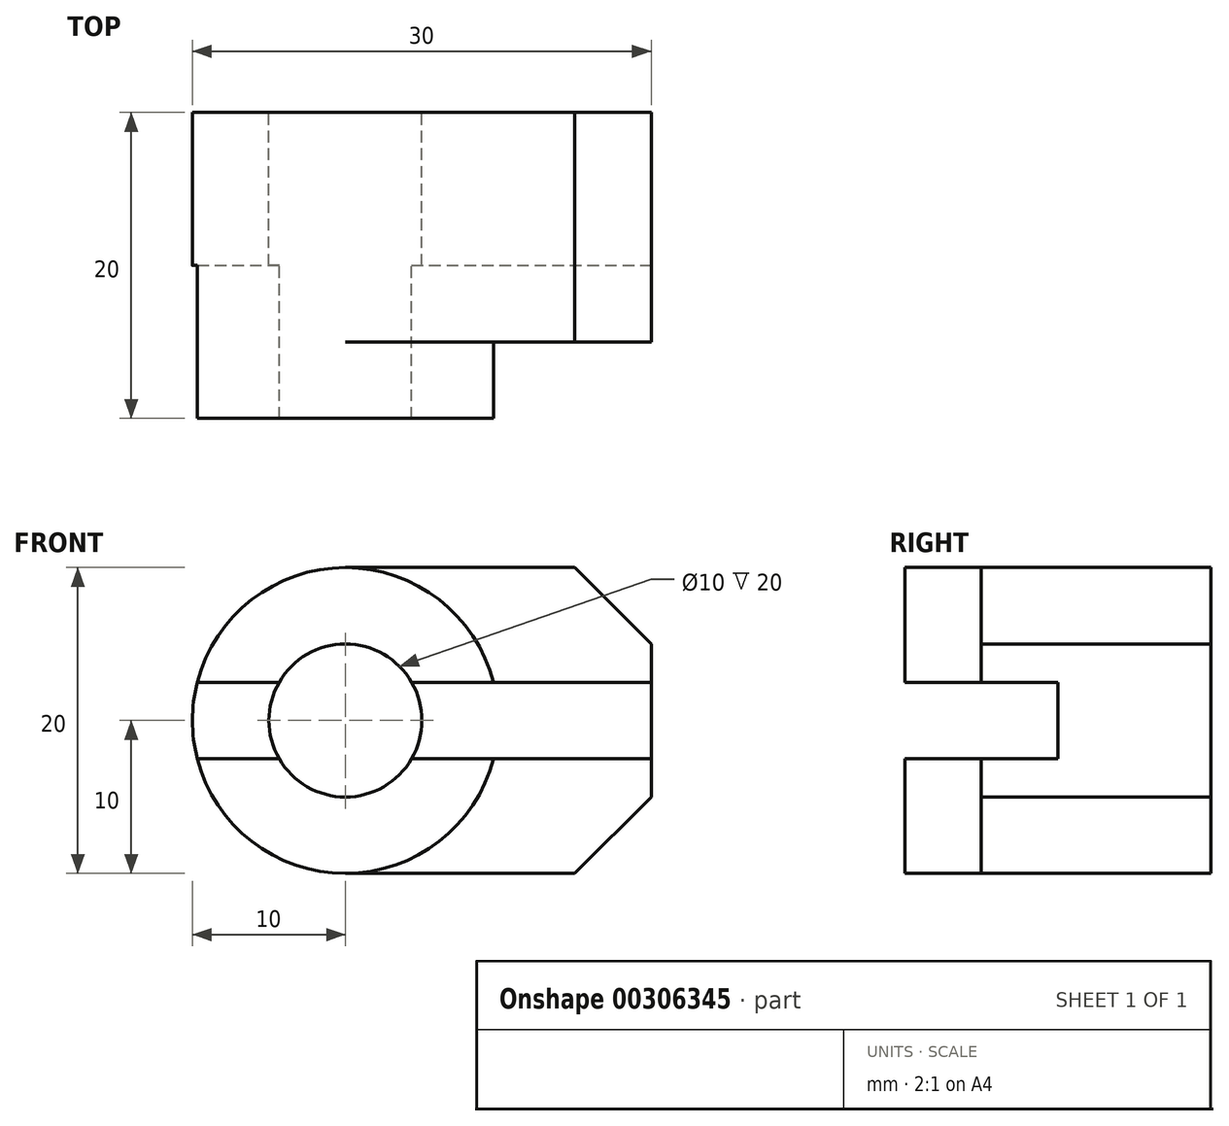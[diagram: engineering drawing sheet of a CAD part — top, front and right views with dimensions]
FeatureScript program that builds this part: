
annotation { "Feature Type Name" : "Feature", "Feature Type Description" : "" }
export const myFeature = defineFeature(function(context is Context, id is Id, definition is map)
    precondition{}
    {
        {
            var Q0;
            Q0=qCreatedBy(makeId("Front.planeOp"),FACE);
            var sketch = newSketch(context, id + "F0", { "sketchPlane" : qUnion([Q0])});
            skCircle(sketch, "E0", {"center": v(0, 0) * mm, "radius": 10 * mm});
            skLineSegment(sketch, "E1", {"start": v(0, 10) * mm, "end": v(15, 10) * mm});
            skLineSegment(sketch, "E2", {"start": v(15, 10) * mm, "end": v(20, 5) * mm});
            skLineSegment(sketch, "E3", {"start": v(20, 5) * mm, "end": v(20, -5) * mm});
            skLineSegment(sketch, "E4", {"start": v(20, -5) * mm, "end": v(15, -10) * mm});
            skLineSegment(sketch, "E5", {"start": v(15, -10) * mm, "end": v(0, -10) * mm});
            skPoint(sketch, "E6", {"position": v(0, -10) * mm});
            skCircle(sketch, "E7", {"center": v(0, 0) * mm, "radius": 5 * mm});
            skPoint(sketch, "E8", {"position": v(0, 5) * mm});
            skPoint(sketch, "E9", {"position": v(0, -5) * mm});
            skSolve(sketch);
        }
        {
            var Q0;
            Q0=makeQuery(id+"F0.imprint","IMPRINT",FACE,{"disambiguationData":[TD([[makeQuery(id+"F0.imprint","IMPRINT",EDGE,{"derivedFrom":sQuery(id+"F0.wireOp",EDGE,"E7")}),-1.0]])]});
            extrude(context, id + "F1", {"entities" : qUnion([Q0]), "depth" : 20 * mm});
        }
        {
            var Q0;
            {var subQ0=sQuery(id+"F0.wireOp",EDGE,"E1");Q0=makeQuery(id+"F0.imprint","IMPRINT",FACE,{"disambiguationData":[TD([[makeQuery(id+"F0.imprint","IMPRINT",EDGE,{"derivedFrom":subQ0}),-1.0]])]});}
            extrude(context, id + "F2", {"entities" : qUnion([Q0]), "operationType" : NewBodyOperationType.ADD, "depth" : 15 * mm});
        }
        {
            var Q0;
            Q0=makeQuery(id+"F2.opExtrude","SWEPT_FACE",FACE,{"disambiguationData":[OSD([sQuery(id+"F0.wireOp",EDGE,"E3")])]});
            var sketch = newSketch(context, id + "F3", { "sketchPlane" : qUnion([Q0])});
            skLineSegment(sketch, "E10.bottom", {"start": v(-10, 2.5) * mm, "end": v(-20, 2.5) * mm});
            skLineSegment(sketch, "E10.top", {"start": v(-10, -2.5) * mm, "end": v(-20, -2.5) * mm});
            skLineSegment(sketch, "E10.left", {"start": v(-10, 2.5) * mm, "end": v(-10, -2.5) * mm});
            skLineSegment(sketch, "E10.right", {"start": v(-20, 2.5) * mm, "end": v(-20, -2.5) * mm});
            skSolve(sketch);
        }
        {
            var Q0;
            Q0 = qSketchRegion(id + "F3", true);
            extrude(context, id + "F4", {"entities" : qUnion([Q0]), "operationType" : NewBodyOperationType.REMOVE, "endBound" : BoundingType.THROUGH_ALL, "oppositeDirection" : true, "depth" : 25 * mm});
        }
    });
